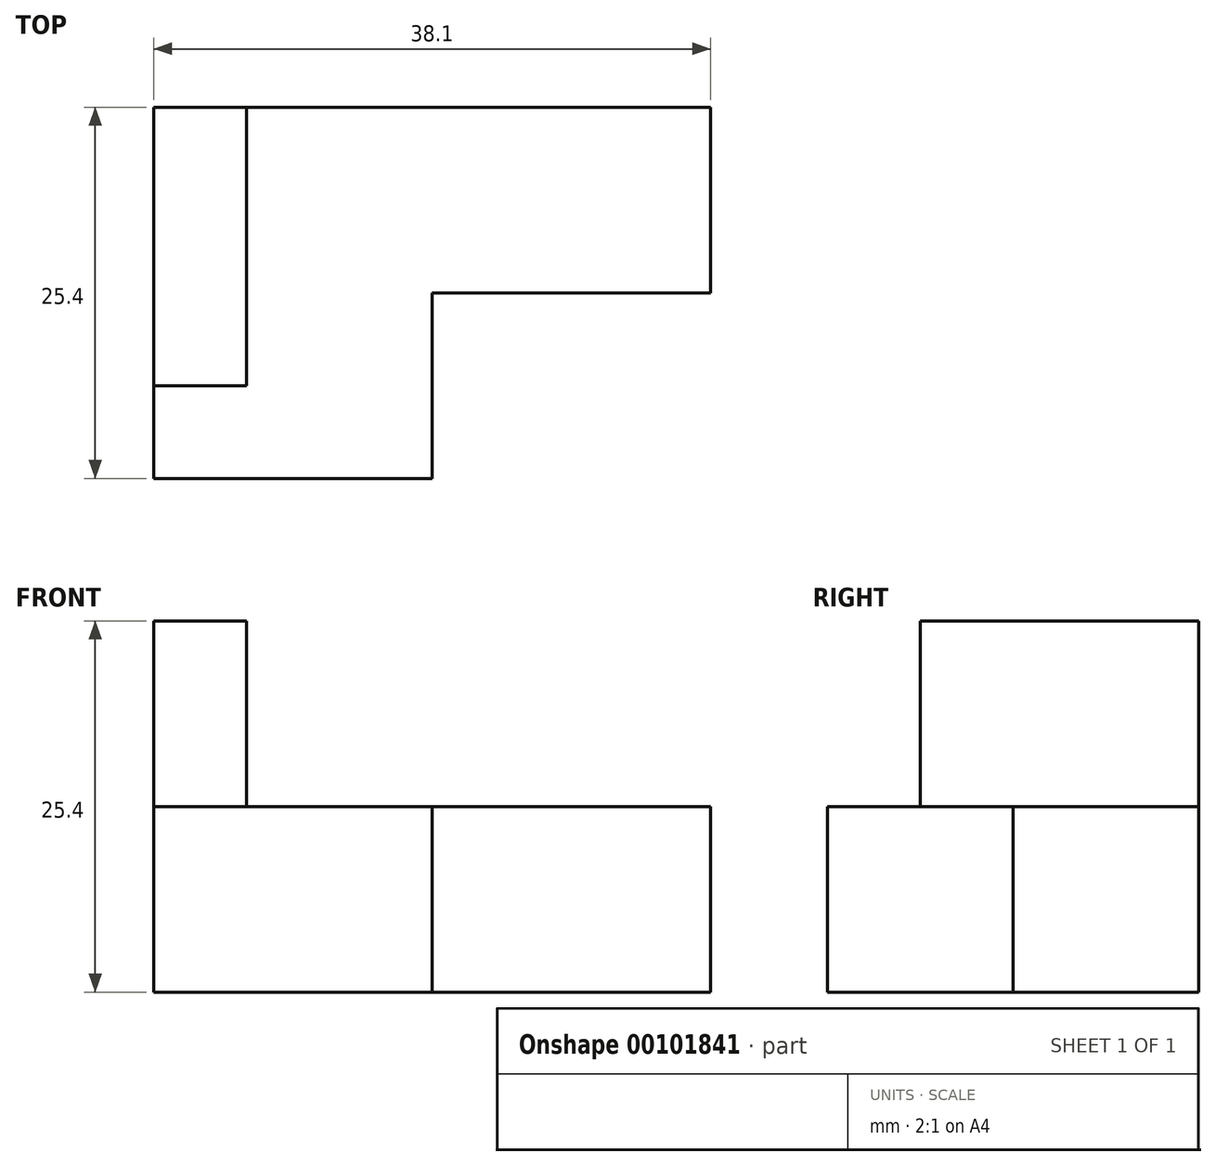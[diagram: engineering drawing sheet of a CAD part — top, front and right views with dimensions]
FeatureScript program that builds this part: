
annotation { "Feature Type Name" : "Feature", "Feature Type Description" : "" }
export const myFeature = defineFeature(function(context is Context, id is Id, definition is map)
    precondition{}
    {
        {
            var Q0;
            Q0=qCreatedBy(makeId("Top.planeOp"),FACE);
            var sketch = newSketch(context, id + "F0", { "sketchPlane" : qUnion([Q0])});
            skLineSegment(sketch, "E0", {"start": v(0, 0) * mm, "end": v(38.1, 0) * mm});
            skLineSegment(sketch, "E1", {"start": v(38.1, 0) * mm, "end": v(38.1, -12.7) * mm});
            skLineSegment(sketch, "E2", {"start": v(38.1, -12.7) * mm, "end": v(19.05, -12.7) * mm});
            skLineSegment(sketch, "E3", {"start": v(19.05, -12.7) * mm, "end": v(19.05, -25.4) * mm});
            skLineSegment(sketch, "E4", {"start": v(19.05, -25.4) * mm, "end": v(0, -25.4) * mm});
            skLineSegment(sketch, "E5", {"start": v(0, -25.4) * mm, "end": v(0, 0) * mm});
            skSolve(sketch);
        }
        {
            var Q0;
            Q0 = qSketchRegion(id + "F0", true);
            extrude(context, id + "F1", {"entities" : qUnion([Q0]), "oppositeDirection" : true, "depth" : 12.7 * mm});
        }
        {
            var Q0;
            Q0=qCreatedBy(makeId("Top.planeOp"),FACE);
            var sketch = newSketch(context, id + "F2", { "sketchPlane" : qUnion([Q0])});
            skLineSegment(sketch, "E6", {"start": v(0, 0) * mm, "end": v(6.35, 0) * mm});
            skLineSegment(sketch, "E7", {"start": v(6.35, 0) * mm, "end": v(6.35, -19.05) * mm});
            skLineSegment(sketch, "E8", {"start": v(6.35, -19.05) * mm, "end": v(0, -19.05) * mm});
            skLineSegment(sketch, "E9", {"start": v(0, -19.05) * mm, "end": v(0, 0) * mm});
            skSolve(sketch);
        }
        {
            var Q0;
            Q0 = qSketchRegion(id + "F2", true);
            extrude(context, id + "F3", {"entities" : qUnion([Q0]), "operationType" : NewBodyOperationType.ADD, "depth" : 12.7 * mm});
        }
    });
